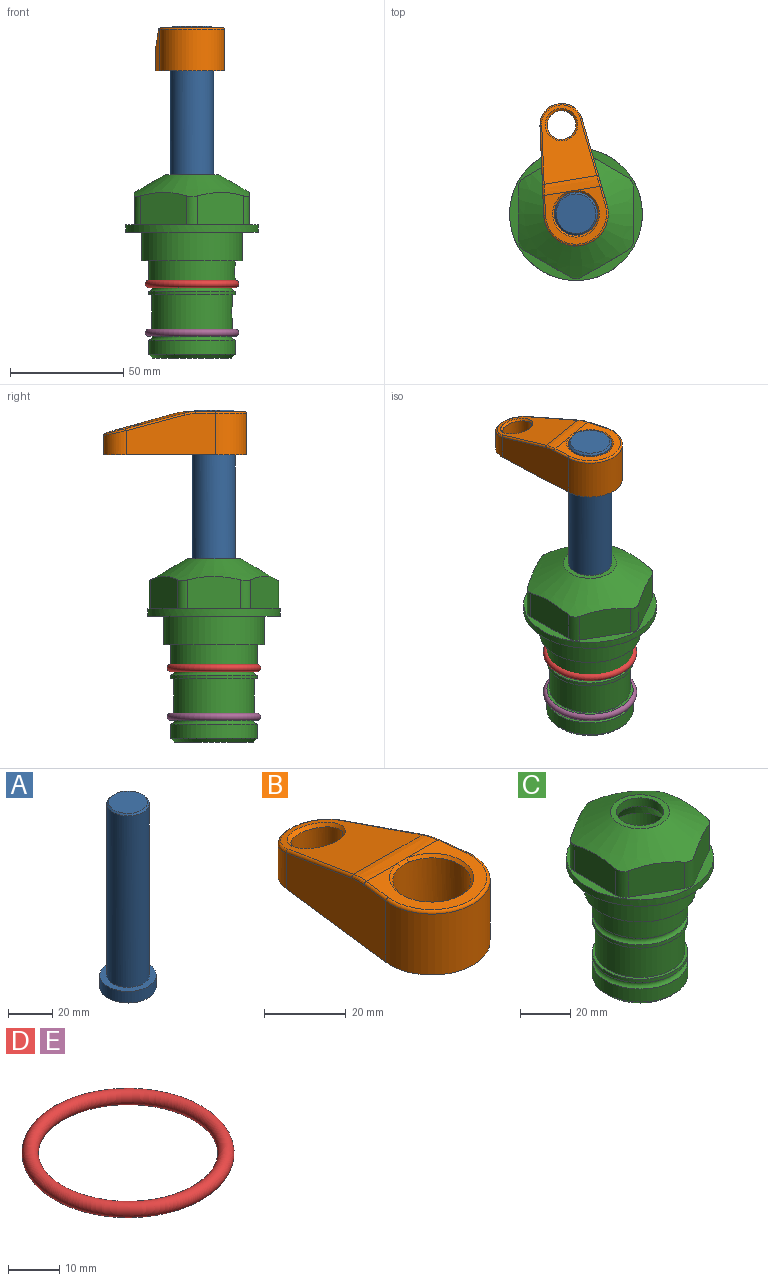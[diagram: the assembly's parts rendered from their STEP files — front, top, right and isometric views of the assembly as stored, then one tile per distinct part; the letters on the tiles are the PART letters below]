
ASSEMBLY  parts=5 mates=4
PART A: 6 faces, bbox 25.4x25.4x101.6 mm
  f0: plane 17.46x17.46mm, normal (0,0,1), area 239.5mm2, adj f5
  f1: plane 25.4x25.4mm, normal (0,0,-1), area 506.7mm2, adj f2
  f2: cylinder r=12.7mm len=25.4mm, axis (0,0,1), area 506.7mm2, adj f1,f3
  f3: plane 25.4x25.4mm, normal (0,0,1), area 221.7mm2, adj f2,f4
  f4: cylinder r=9.53mm len=94.46mm, axis (0,0,1), area 5653mm2, adj f3,f5
  f5: cone r=8.73mm half-angle=45deg, axis (0,0,-1), area 64.4mm2, adj f0,f4
PART B: 31 faces, bbox 31.7x65.5x19.8 mm
  f0: plane 39.12x18.26mm, normal (0.99,0.12,0), area 612.2mm2, adj f1,f4,f7,f11,f13,f15
  f1: cylinder r=9.53mm len=18.91mm, axis (0,0,-1), area 296.1mm2, adj f0,f2,f7,f17
  f2: plane 39.12x18.26mm, normal (-0.99,0.12,0), area 612.2mm2, adj f1,f4,f7,f12,f14,f16
  f3: cylinder r=6.35mm len=12.7mm, axis (0,0,-1), area 362.4mm2, adj f7,f18
  f4: cylinder r=14.29mm len=28.58mm, axis (0,0,-1), area 882.2mm2, adj f0,f2,f7,f10
  f5: cylinder r=9.53mm len=19.05mm, axis (0,0,-1), area 1092.6mm2, adj f7,f19,f20
  f6: plane 26.99x23.69mm, normal (0,0,1), area 216.2mm2, adj f9,f10,f11,f12,f19
  f7: plane 63.5x28.58mm, normal (0,0,-1), area 661.8mm2, adj f0,f1,f2,f3,f4,f5,f22,f23
  f8: plane 33.52x23.6mm, normal (0,0.26,0.97), area 486mm2, adj f9,f15,f16,f17,f18
  f9: cylinder r=19.05mm len=24.72mm, axis (1,0,0), area 120.4mm2, adj f6,f8,f13,f14,f20
  f10: torus R=13.49mm, axis (0,0,1), area 59mm2, adj f4,f6,f11,f12
  f11: cylinder r=0.79mm len=8.67mm, axis (0.12,-0.99,0), area 10.8mm2, adj f0,f6,f10,f13
  f12: cylinder r=0.79mm len=8.67mm, axis (0.12,0.99,0), area 10.8mm2, adj f2,f6,f10,f14
  f13: bspline ~4.95x1.42mm, area 6.1mm2, adj f0,f9,f11,f15
  f14: bspline ~4.95x1.42mm, area 6.1mm2, adj f2,f9,f12,f16
  f15: cylinder r=0.79mm len=25.95mm, axis (0.12,-0.96,0.26), area 32.9mm2, adj f0,f8,f13,f17
  f16: cylinder r=0.79mm len=25.95mm, axis (0.12,0.96,-0.26), area 32.9mm2, adj f2,f8,f14,f17
  f17: bspline ~18.91x8.38mm, area 30mm2, adj f1,f8,f15,f16
  f18: bspline ~14.29x14.29mm, area 48.3mm2, adj f3,f8
  f19: cone r=9.53mm half-angle=45deg, axis (0,0,1), area 66.5mm2, adj f5,f6,f20
  f20: bspline ~3.22x0.96mm, area 3.5mm2, adj f5,f9,f19
  f21: plane 2.75x2.72mm, normal (0,0,-1), area 2.9mm2, adj f23,f25,f28
  f22: plane 23.05x15.88mm, normal (-0.99,-0.12,0), area 323.6mm2, adj f7,f25,f26,f27,f28,f29
  f23: plane 23.05x15.88mm, normal (0.99,-0.12,0), area 323.6mm2, adj f7,f21,f25,f27,f28,f30
  f24: cylinder r=9.53mm len=10.69mm, axis (0,0,-1), area 114.7mm2, adj f7,f27,f29,f30
  f25: cylinder r=12.7mm len=20.59mm, axis (0,0,-1), area 381.1mm2, adj f7,f21,f22,f23,f26,f28
  f26: plane 2.75x2.72mm, normal (0,0,-1), area 2.9mm2, adj f22,f25,f28
  f27: plane 19.72x18.37mm, normal (0,-0.26,-0.97), area 291.8mm2, adj f22,f23,f24,f28,f29,f30
  f28: cylinder r=15.88mm len=19.92mm, axis (1,0,0), area 54.8mm2, adj f21,f22,f23,f25,f26,f27
  f29: cylinder r=1.59mm len=11mm, axis (0,0,-1), area 34.7mm2, adj f7,f22,f24,f27
  f30: cylinder r=1.59mm len=11mm, axis (0,0,-1), area 34.7mm2, adj f7,f23,f24,f27
PART C: 36 faces, bbox 58.7x58.7x81 mm
  f0: cylinder r=17.78mm len=35.56mm, axis (0,0,1), area 1670.8mm2, adj f23,f24,f31
  f1: cylinder r=19.05mm len=38.1mm, axis (0,0,1), area 1191.9mm2, adj f26,f27,f30
  f2: plane 58.66x58.66mm, normal (0,0,-1), area 1150.6mm2, adj f3,f28
  f3: cylinder r=29.33mm len=58.66mm, axis (0,0,-1), area 585.1mm2, adj f2,f4
  f4: plane 58.66x58.66mm, normal (0,0,1), area 475.9mm2, adj f3,f5,f6,f7,f8,f9,f10,f11
  f5: plane 20.32x14.34mm, normal (-0.5,0.87,0), area 324.4mm2, adj f4,f15,f16,f17
  f6: plane 20.32x14.34mm, normal (0.5,0.87,0), area 324.4mm2, adj f4,f14,f15,f17
  f7: plane 23.48x14.34mm, normal (1,0,0), area 324.4mm2, adj f4,f13,f14,f17
  f8: plane 20.32x14.34mm, normal (0.5,-0.87,0), area 324.4mm2, adj f4,f12,f13,f17
  f9: plane 20.32x14.34mm, normal (-0.5,-0.87,0), area 324.4mm2, adj f4,f11,f12,f17
  f10: plane 23.48x14.34mm, normal (-1,0,0), area 324.4mm2, adj f4,f11,f16,f17
  f11: cylinder r=5.08mm len=12.85mm, axis (0,0,-1), area 67.2mm2, adj f4,f9,f10,f17
  f12: cylinder r=5.08mm len=12.85mm, axis (0,0,-1), area 67.2mm2, adj f4,f8,f9,f17
  f13: cylinder r=5.08mm len=12.85mm, axis (0,0,-1), area 67.2mm2, adj f4,f7,f8,f17
  f14: cylinder r=5.08mm len=12.85mm, axis (0,0,-1), area 67.2mm2, adj f4,f6,f7,f17
  f15: cylinder r=5.08mm len=12.85mm, axis (0,0,-1), area 67.2mm2, adj f4,f5,f6,f17
  f16: cylinder r=5.08mm len=12.85mm, axis (0,0,-1), area 67.2mm2, adj f4,f5,f10,f17
  f17: cone r=11.73mm half-angle=60deg, axis (0,0,-1), area 2071.8mm2, adj f5,f6,f7,f8,f9,f10,f11,f12
  f18: plane 23.46x23.46mm, normal (0,0,1), area 147.4mm2, adj f17,f35
  f19: plane 34.93x34.93mm, normal (0,0,-1), area 958mm2, adj f29
  f20: cylinder r=19.05mm len=38.1mm, axis (0,0,1), area 760.1mm2, adj f21,f29
  f21: torus R=19.05mm, axis (0,0,1), area 565.3mm2, adj f20,f22
  f22: cylinder r=19.05mm len=38.1mm, axis (0,0,1), area 190mm2, adj f21,f23
  f23: plane 38.1x38.1mm, normal (0,0,1), area 146.9mm2, adj f0,f22
  f24: plane 38.1x38.1mm, normal (0,0,-1), area 146.9mm2, adj f0,f25
  f25: cylinder r=19.05mm len=38.1mm, axis (0,0,1), area 190mm2, adj f24,f26
  f26: torus R=19.05mm, axis (0,0,1), area 565.3mm2, adj f1,f25
  f27: plane 44.45x44.45mm, normal (0,0,-1), area 411.7mm2, adj f1,f28
  f28: cylinder r=22.23mm len=44.45mm, axis (0,0,1), area 1773.5mm2, adj f2,f27
  f29: cone r=19.05mm half-angle=45deg, axis (0,0,1), area 257.5mm2, adj f19,f20
  f30: cylinder r=3.17mm len=6.75mm, axis (-1,0,0), area 128mm2, adj f1,f33
  f31: cylinder r=3.17mm len=6.35mm, axis (-1,0,0), area 102.5mm2, adj f0,f33
  f32: plane 25.4x25.4mm, normal (0,0,1), area 506.7mm2, adj f33
  f33: cylinder r=12.7mm len=66.42mm, axis (0,0,-1), area 5236.2mm2, adj f30,f31,f32,f34
  f34: cone r=9.53mm half-angle=30deg, axis (0,0,-1), area 443.4mm2, adj f33,f35
  f35: cylinder r=9.53mm len=19.05mm, axis (0,0,-1), area 240.9mm2, adj f18,f34
PART D: 1 faces, bbox 44.7x44.7x3.2 mm
  f0: torus R=19.05mm, axis (0,0,1), area 1193.9mm2
PART E: same geometry as D
PLACE A rot(axis=(0,0,1),9.3deg) t=(0,0,27.55)mm
PLACE B rot(axis=(0,0,1),9.3deg) t=(0,0,26.76)mm
PLACE C at identity fixed
PLACE D t=(0,0,1.59)mm
PLACE E t=(0,0,-20)mm
MATE fastened D.f0 <-> C.f0  axis (0,0,1) through (0,0,-22.92)mm
MATE fastened C.f0 <-> E.f0  axis (0,0,1) through (0,0,-44.51)mm
MATE fastened B.f4 <-> A.f2  axis (0,0,1) through (0,0,90.26)mm
MATE cylindrical C.f0 <-> A.f2  axis (0,0,1) through (0,0,-50.55)mm
